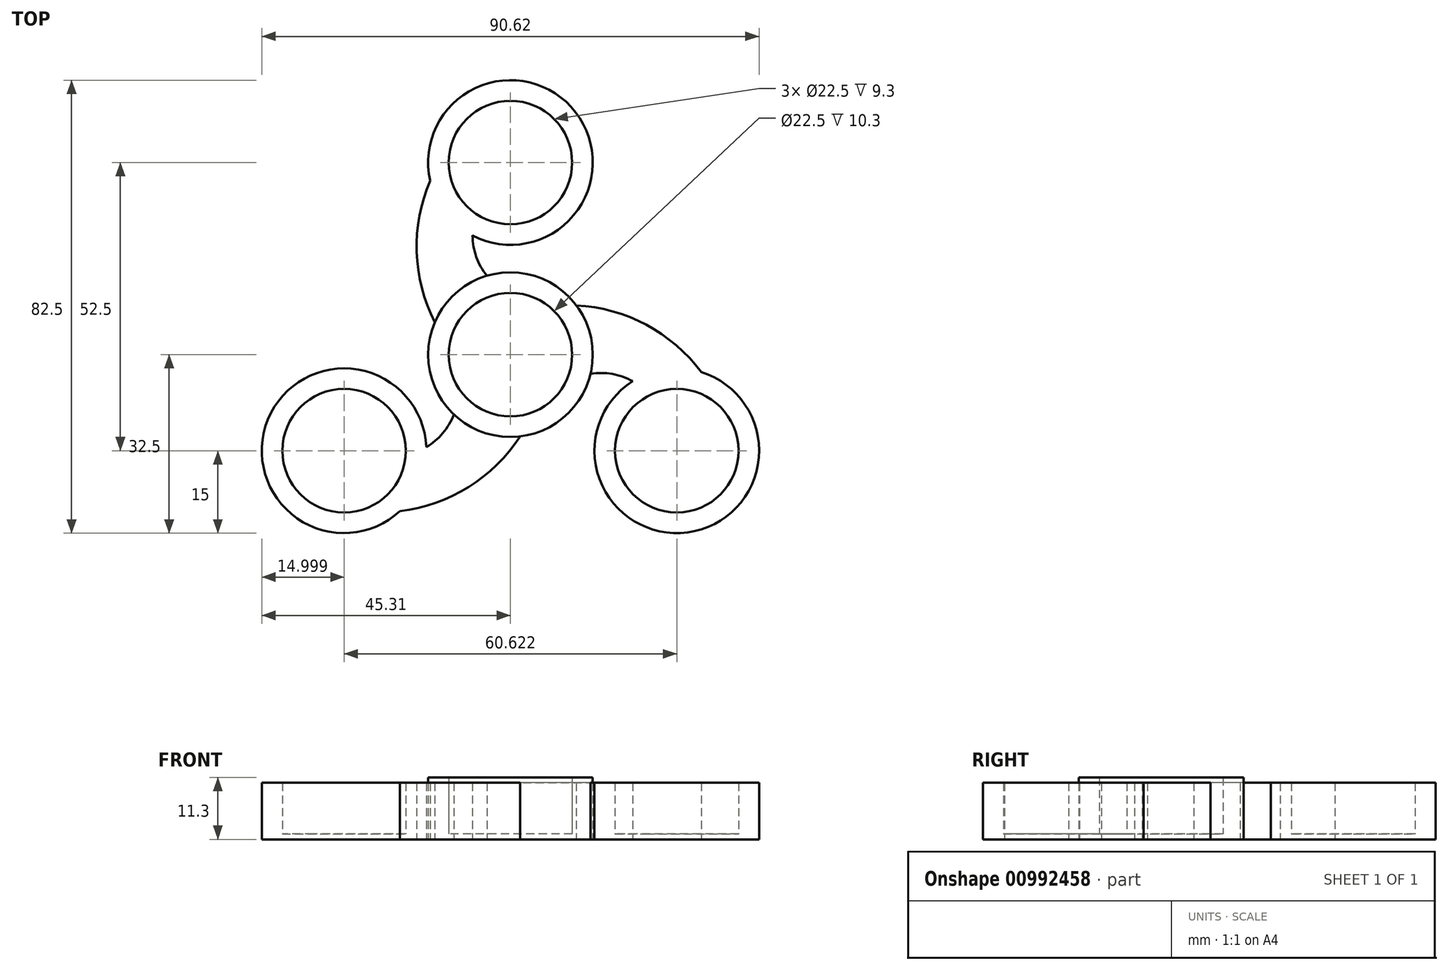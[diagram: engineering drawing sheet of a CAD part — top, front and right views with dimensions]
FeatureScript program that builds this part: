
annotation { "Feature Type Name" : "Feature", "Feature Type Description" : "" }
export const myFeature = defineFeature(function(context is Context, id is Id, definition is map)
    precondition{}
    {
        {
            var Q0;
            Q0=qCreatedBy(makeId("Top.planeOp"),FACE);
            var sketch = newSketch(context, id + "F0", { "sketchPlane" : qUnion([Q0])});
            skCircle(sketch, "E0", {"center": v(0, 0) * mm, "radius": 11.25 * mm});
            skCircle(sketch, "E1", {"center": v(0, 35) * mm, "radius": 11.25 * mm});
            skCircle(sketch, "E2", {"center": v(0, 0) * mm, "radius": 15 * mm});
            skCircle(sketch, "E3", {"center": v(0, 35) * mm, "radius": 15 * mm});
            skArc(sketch, "E4", {"start": v(-14.63, 31.69) * mm, "mid": v(-17.08, 18.7) * mm, "end": v(-13.79, 5.91) * mm});
            skArc(sketch, "E5", {"start": v(-6.92, 21.7) * mm, "mid": v(-6.22, 17.8) * mm, "end": v(-4.28, 14.38) * mm});
            skSolve(sketch);
        }
        {
            var Q0;
            Q0=makeQuery(id+"F0.imprint","IMPRINT",FACE,{"disambiguationData":[TD([[makeQuery(id+"F0.imprint","IMPRINT",EDGE,{"derivedFrom":sQuery(id+"F0.wireOp",EDGE,"E0")}),-1.0]])]});
            extrude(context, id + "F1", {"entities" : qUnion([Q0]), "depth" : 11.3 * mm, "offsetDistance" : 25 * mm});
        }
        {
            var Q0;
            {var subQ0=sQuery(id+"F0.wireOp",EDGE,"E4");Q0=makeQuery(id+"F0.imprint","IMPRINT",FACE,{"disambiguationData":[TD([[makeQuery(id+"F0.imprint","IMPRINT",EDGE,{"derivedFrom":subQ0}),1.0]])]});}
            var Q1;
            Q1=makeQuery(id+"F0.imprint","IMPRINT",FACE,{"disambiguationData":[TD([[makeQuery(id+"F0.imprint","IMPRINT",EDGE,{"derivedFrom":sQuery(id+"F0.wireOp",EDGE,"E1")}),-1.0]])]});
            extrude(context, id + "F2", {"entities" : qUnion([Q0, Q1]), "depth" : 10.3 * mm, "offsetDistance" : 25 * mm});
        }
        {
            var Q0;
            Q0=makeQuery(id+"F0.imprint","IMPRINT",FACE,{"disambiguationData":[TD([[makeQuery(id+"F0.imprint","IMPRINT",EDGE,{"derivedFrom":sQuery(id+"F0.wireOp",EDGE,"E1")}),1.0]])]});
            var Q1;
            Q1=makeQuery(id+"F0.imprint","IMPRINT",FACE,{"disambiguationData":[TD([[makeQuery(id+"F0.imprint","IMPRINT",EDGE,{"derivedFrom":sQuery(id+"F0.wireOp",EDGE,"E0")}),1.0]])]});
            extrude(context, id + "F3", {"entities" : qUnion([Q0, Q1]), "operationType" : NewBodyOperationType.ADD, "depth" : 1 * mm, "offsetDistance" : 25 * mm});
        }
        {
            var Q0;
            Q0=makeQuery(id+"F2.opExtrude","SWEPT_BODY",BODY,{"disambiguationData":[OSD([sQuery(id+"F0.wireOp",EDGE,"E1"),sQuery(id+"F0.wireOp",EDGE,"E2"),sQuery(id+"F0.wireOp",EDGE,"E3"),sQuery(id+"F0.wireOp",EDGE,"E4"),sQuery(id+"F0.wireOp",EDGE,"E5")])]});
            var Q1;
            Q1=makeQuery(id+"F1.opExtrude","CAP_EDGE",EDGE,{"disambiguationData":[OSD([sQuery(id+"F0.wireOp",EDGE,"E2")])],"isStart":false});
            circularPattern(context, id + "F4", {"entities" : qUnion([Q0]), "axis" : qUnion([Q1]), "angle" : 360 * degree, "instanceCount" : 3, "equalSpace" : true});
        }
    });
